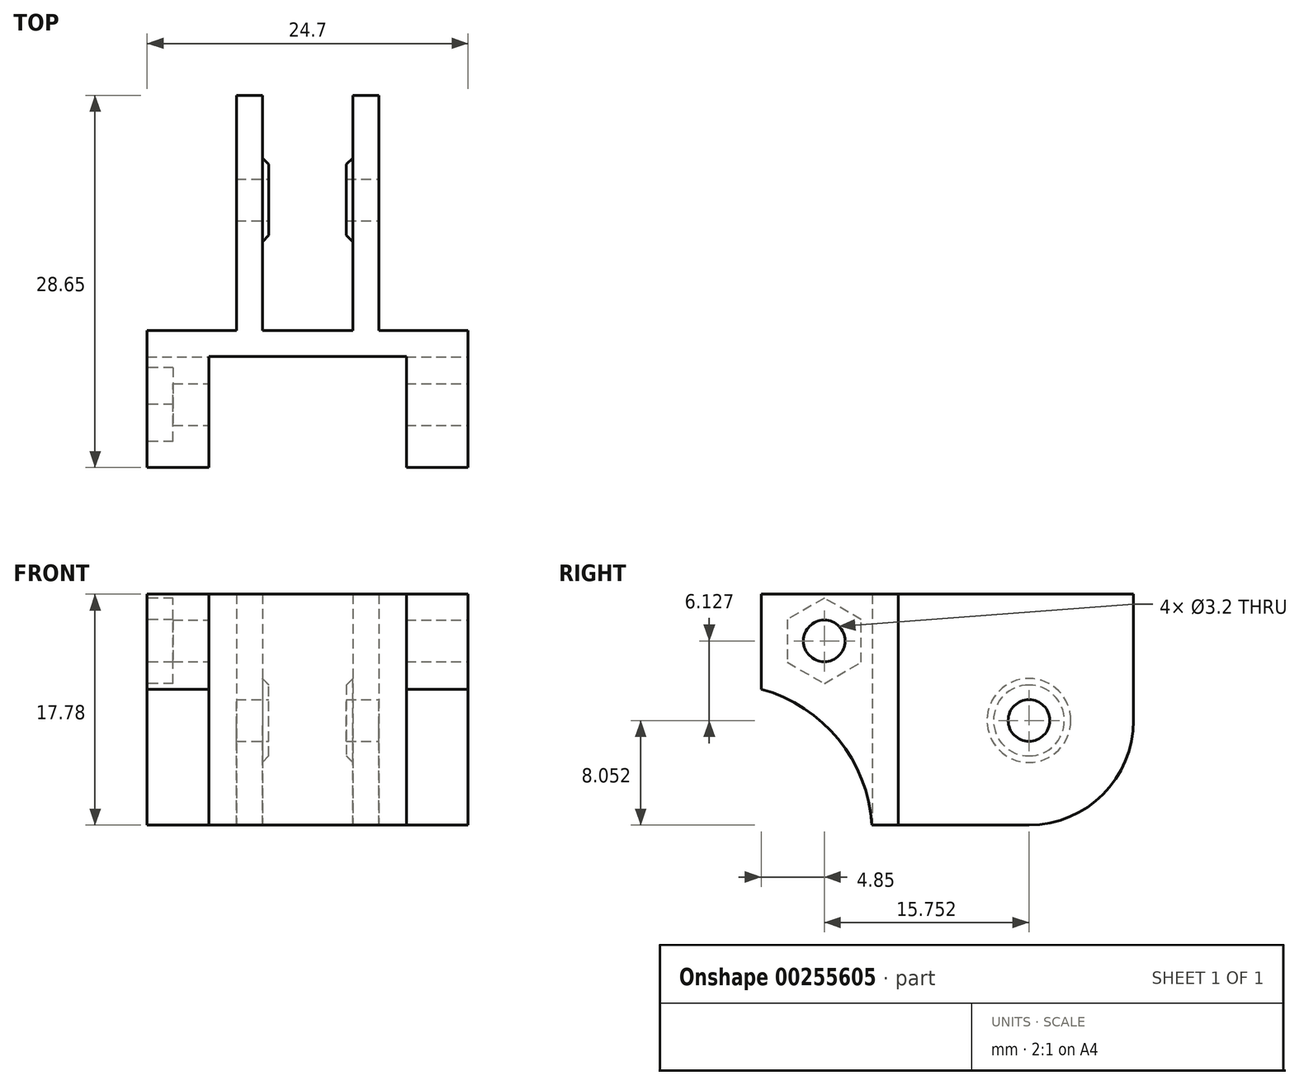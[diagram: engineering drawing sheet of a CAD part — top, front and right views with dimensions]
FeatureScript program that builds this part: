
annotation { "Feature Type Name" : "Feature", "Feature Type Description" : "" }
export const myFeature = defineFeature(function(context is Context, id is Id, definition is map)
    precondition{}
    {
        {
            var Q0;
            Q0=qCreatedBy(makeId("Top.planeOp"),FACE);
            var sketch = newSketch(context, id + "F0", { "sketchPlane" : qUnion([Q0])});
            skLineSegment(sketch, "E0", {"start": v(-3.48, 23.8) * mm, "end": v(-5.48, 23.8) * mm});
            skLineSegment(sketch, "E1", {"start": v(-5.48, 23.8) * mm, "end": v(-5.48, 5.7) * mm});
            skLineSegment(sketch, "E2", {"start": v(-5.48, 5.7) * mm, "end": v(-12.35, 5.7) * mm});
            skLineSegment(sketch, "E3", {"start": v(-12.35, 5.7) * mm, "end": v(-12.35, -4.85) * mm});
            skLineSegment(sketch, "E4", {"start": v(-12.35, -4.85) * mm, "end": v(-7.6, -4.85) * mm});
            skLineSegment(sketch, "E5", {"start": v(-7.6, -4.85) * mm, "end": v(-7.6, 3.7) * mm});
            skLineSegment(sketch, "E6", {"start": v(-7.6, 3.7) * mm, "end": v(7.6, 3.7) * mm});
            skLineSegment(sketch, "E7", {"start": v(-3.48, 23.8) * mm, "end": v(-3.48, 5.7) * mm});
            skLineSegment(sketch, "E8", {"start": v(-3.48, 5.7) * mm, "end": v(3.48, 5.7) * mm});
            skLineSegment(sketch, "E9.MirrorCS", {"start": v(3.48, 23.8) * mm, "end": v(5.48, 23.8) * mm});
            skLineSegment(sketch, "E10.MirrorCS", {"start": v(5.48, 23.8) * mm, "end": v(5.48, 5.7) * mm});
            skLineSegment(sketch, "E11.MirrorCS", {"start": v(3.48, 23.8) * mm, "end": v(3.48, 5.7) * mm});
            skLineSegment(sketch, "E12.MirrorCS", {"start": v(5.48, 5.7) * mm, "end": v(12.35, 5.7) * mm});
            skLineSegment(sketch, "E13.MirrorCS", {"start": v(12.35, 5.7) * mm, "end": v(12.35, -4.85) * mm});
            skLineSegment(sketch, "E14.MirrorCS", {"start": v(12.35, -4.85) * mm, "end": v(7.6, -4.85) * mm});
            skLineSegment(sketch, "E15.MirrorCS", {"start": v(7.6, -4.85) * mm, "end": v(7.6, 3.7) * mm});
            skLineSegment(sketch, "E16", {"start": v(-14.8, 0) * mm, "end": v(23.59, 0) * mm, "construction": true});
            skSolve(sketch);
        }
        {
            var Q0;
            Q0 = qSketchRegion(id + "F0", true);
            extrude(context, id + "F1", {"entities" : qUnion([Q0]), "depth" : 25 * mm - 7.22 * mm});
        }
        {
            var Q0;
            Q0=makeQuery(id+"F1.opExtrude","SWEPT_FACE",FACE,{"disambiguationData":[OSD([sQuery(id+"F0.wireOp",EDGE,"E13.MirrorCS")])]});
            var sketch = newSketch(context, id + "F2", { "sketchPlane" : qUnion([Q0])});
            skArc(sketch, "E17", {"start": v(3.7, -0.74) * mm, "mid": v(-16.12, 7.47) * mm, "end": v(-7.91, -12.35) * mm});
            skLineSegment(sketch, "E18.0", {"start": v(-4.85, 17.78) * mm, "end": v(-4.85, 10.46) * mm});
            skPoint(sketch, "E19.orphan", {"position": v(-4.85, 0) * mm});
            skLineSegment(sketch, "E20", {"start": v(3.7, -0.74) * mm, "end": v(3.7, -12.35) * mm});
            skLineSegment(sketch, "E21", {"start": v(3.7, -12.35) * mm, "end": v(-7.91, -12.35) * mm});
            skSolve(sketch);
        }
        {
            var Q0;
            Q0 = qSketchRegion(id + "F2", true);
            extrude(context, id + "F3", {"entities" : qUnion([Q0]), "operationType" : NewBodyOperationType.REMOVE, "endBound" : BoundingType.THROUGH_ALL, "oppositeDirection" : true, "depth" : 25 * mm});
        }
        {
            var Q0;
            Q0=makeQuery(id+"F1.opExtrude","SWEPT_FACE",FACE,{"disambiguationData":[OSD([sQuery(id+"F0.wireOp",EDGE,"E10.MirrorCS")])]});
            var sketch = newSketch(context, id + "F4", { "sketchPlane" : qUnion([Q0])});
            skCircle(sketch, "E22", {"center": v(15.75, 8.05) * mm, "radius": 3.33 * mm, "construction": true});
            skCircle(sketch, "E23", {"center": v(15.75, 8.05) * mm, "radius": 8.05 * mm, "construction": true});
            skLineSegment(sketch, "E24", {"start": v(23.8, 17.78) * mm, "end": v(23.8, 8.05) * mm, "construction": true});
            skLineSegment(sketch, "E25", {"start": v(23.8, 17.78) * mm, "end": v(7.7, 17.78) * mm, "construction": true});
            skLineSegment(sketch, "E26", {"start": v(7.7, 8.05) * mm, "end": v(7.7, 17.78) * mm, "construction": true});
            skCircle(sketch, "E27", {"center": v(15.75, 8.05) * mm, "radius": 1.6 * mm});
            skSolve(sketch);
        }
        {
            var Q0;
            Q0 = qSketchRegion(id + "F4", true);
            extrude(context, id + "F5", {"entities" : qUnion([Q0]), "operationType" : NewBodyOperationType.REMOVE, "endBound" : BoundingType.THROUGH_ALL, "oppositeDirection" : true, "depth" : 25 * mm});
        }
        {
            var Q0;
            Q0=makeQuery(id+"F1.opExtrude","SWEPT_FACE",FACE,{"disambiguationData":[OSD([sQuery(id+"F0.wireOp",EDGE,"E13.MirrorCS")])]});
            var sketch = newSketch(context, id + "F6", { "sketchPlane" : qUnion([Q0])});
            skCircle(sketch, "E28", {"center": v(0, 14.18) * mm, "radius": 1.6 * mm});
            skSolve(sketch);
        }
        {
            var Q0;
            Q0 = qSketchRegion(id + "F6", true);
            extrude(context, id + "F7", {"entities" : qUnion([Q0]), "operationType" : NewBodyOperationType.REMOVE, "endBound" : BoundingType.THROUGH_ALL, "oppositeDirection" : true, "depth" : 25 * mm});
        }
        {
            var Q0;
            Q0=makeQuery(id+"F1.opExtrude","SWEPT_FACE",FACE,{"disambiguationData":[OSD([sQuery(id+"F0.wireOp",EDGE,"E3")])]});
            var sketch = newSketch(context, id + "F8", { "sketchPlane" : qUnion([Q0])});
            skCircle(sketch, "E29.cCircle", {"center": v(0, 14.18) * mm, "radius": 2.85 * mm, "construction": true});
            skLineSegment(sketch, "E29.0", {"start": v(-2.85, 15.82) * mm, "end": v(0, 17.47) * mm});
            skLineSegment(sketch, "E29.1", {"start": v(0, 17.47) * mm, "end": v(2.85, 15.82) * mm});
            skLineSegment(sketch, "E29.2", {"start": v(2.85, 15.82) * mm, "end": v(2.85, 12.53) * mm});
            skLineSegment(sketch, "E29.3", {"start": v(2.85, 12.53) * mm, "end": v(0, 10.89) * mm});
            skLineSegment(sketch, "E29.4", {"start": v(0, 10.89) * mm, "end": v(-2.85, 12.53) * mm});
            skLineSegment(sketch, "E29.5", {"start": v(-2.85, 12.53) * mm, "end": v(-2.85, 15.82) * mm});
            skPoint(sketch, "E29.0.midPoint", {"position": v(-1.42, 16.65) * mm});
            skSolve(sketch);
        }
        {
            var Q0;
            Q0 = qSketchRegion(id + "F8", true);
            extrude(context, id + "F9", {"entities" : qUnion([Q0]), "operationType" : NewBodyOperationType.REMOVE, "oppositeDirection" : true, "depth" : 2 * mm});
        }
        {
            var Q0;
            Q0=makeQuery(id+"F1.opExtrude","SWEPT_FACE",FACE,{"disambiguationData":[OSD([sQuery(id+"F0.wireOp",EDGE,"E11.MirrorCS")])]});
            var sketch = newSketch(context, id + "F10", { "sketchPlane" : qUnion([Q0])});
            skCircle(sketch, "E30", {"center": v(-15.75, 8.05) * mm, "radius": 3.23 * mm});
            skSolve(sketch);
        }
        {
            var Q0;
            Q0=makeQuery(id+"F10.imprint","IMPRINT",FACE,{"disambiguationData":[TD([[makeQuery(id+"F10.imprint","IMPRINT",EDGE,{"derivedFrom":sQuery(id+"F10.wireOp",EDGE,"E30")}),1.0]])]});
            extrude(context, id + "F11", {"entities" : qUnion([Q0]), "depth" : .5 * mm});
        }
        {
            var Q0;
            Q0=makeQuery(id+"F11.opExtrude","SWEPT_BODY",BODY,{"disambiguationData":[OSD([sQuery(id+"F0.wireOp",EDGE,"E11.MirrorCS"),sQuery(id+"F4.wireOp",EDGE,"E27"),sQuery(id+"F10.wireOp",EDGE,"E30")])]});
            var Q1;
            Q1=qCreatedBy(makeId("Right.planeOp"),FACE);
            mirror(context, id + "F12", {"operationType" : NewBodyOperationType.ADD, "entities" : qUnion([Q0]), "mirrorPlane" : qUnion([Q1])});
        }
        {
            var Q0;
            Q0=makeQuery(id+"F11.opExtrude","CAP_EDGE",EDGE,{"disambiguationData":[OSD([sQuery(id+"F10.wireOp",EDGE,"E30")])],"isStart":false});
            var Q1;
            Q1=makeQuery(id+"F12.opPattern","COPY",EDGE,{"derivedFrom":makeQuery(id+"F11.opExtrude","CAP_EDGE",EDGE,{"disambiguationData":[OSD([sQuery(id+"F10.wireOp",EDGE,"E30")])],"isStart":false}),"instanceName":"1"});
            chamfer(context, id + "F13", {"entities" : qUnion([Q0, Q1]), "width" : .5 * mm, "tangentPropagation" : true});
        }
        {
            var Q0;
            Q0=makeQuery(id+"F1.opExtrude","CAP_EDGE",EDGE,{"disambiguationData":[OSD([sQuery(id+"F0.wireOp",EDGE,"E0")])],"isStart":true});
            var Q1;
            Q1=makeQuery(id+"F1.opExtrude","CAP_EDGE",EDGE,{"disambiguationData":[OSD([sQuery(id+"F0.wireOp",EDGE,"E9.MirrorCS")])],"isStart":true});
            fillet(context, id + "F14", {"entities" : qUnion([Q0, Q1]), "radius" : (16.1 / 2) * mm, "tangentPropagation" : true, "allowEdgeOverflow" : false});
        }
    });
